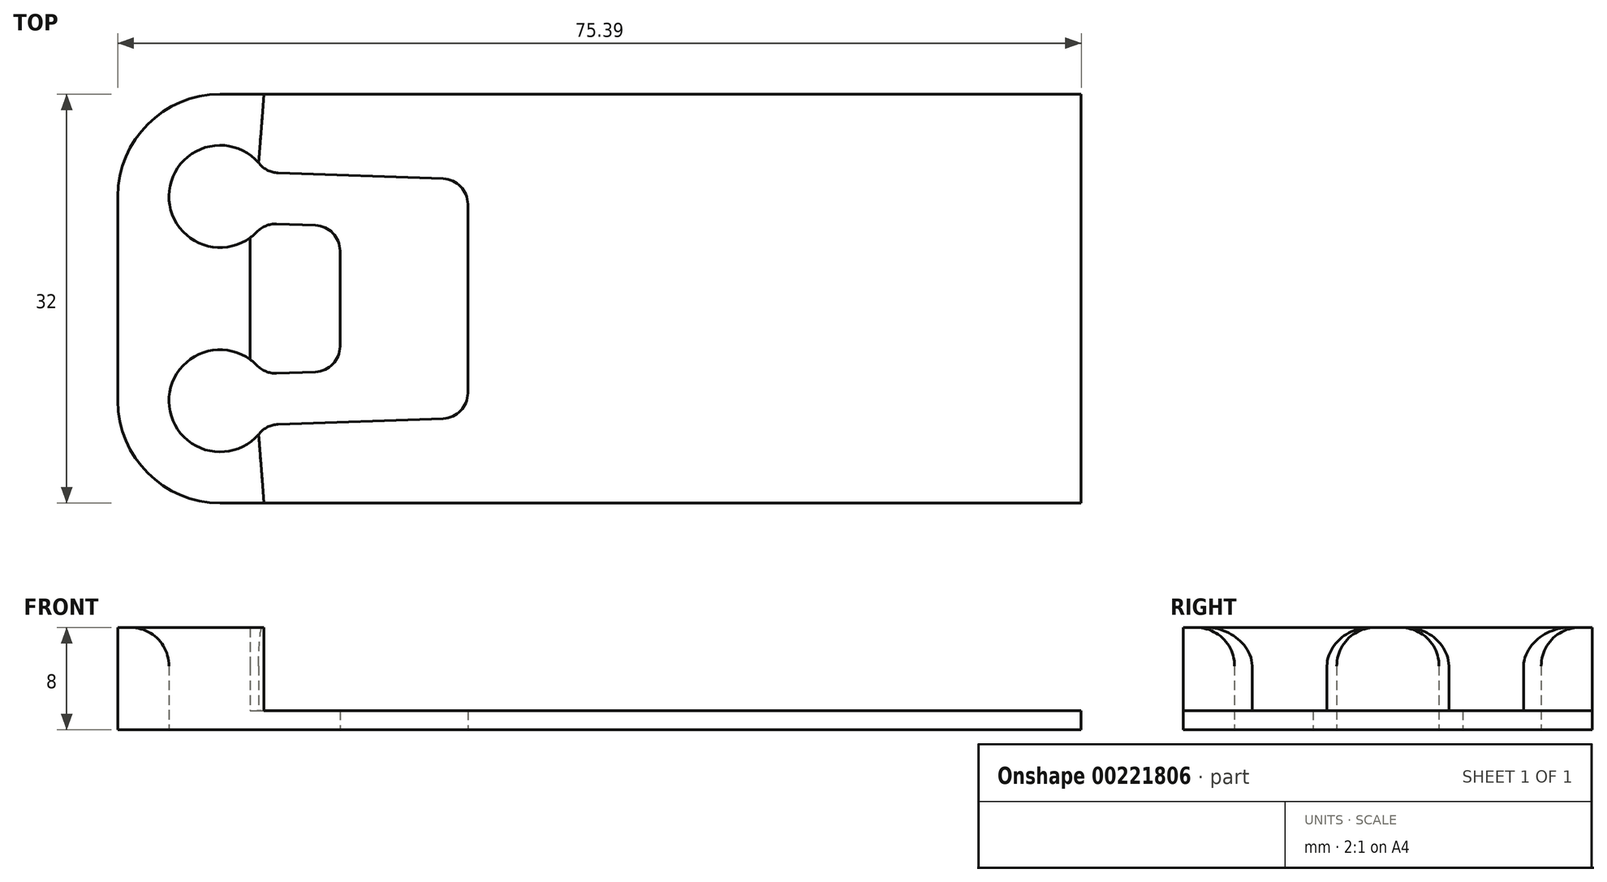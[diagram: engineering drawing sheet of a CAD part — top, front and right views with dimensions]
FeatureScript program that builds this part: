
annotation { "Feature Type Name" : "Feature", "Feature Type Description" : "" }
export const myFeature = defineFeature(function(context is Context, id is Id, definition is map)
    precondition{}
    {
        {
            var Q0;
            Q0=qCreatedBy(makeId("Top.planeOp"),FACE);
            var sketch = newSketch(context, id + "F0", { "sketchPlane" : qUnion([Q0])});
            skEllipse(sketch, "E0", {"center": v(381, 0) * mm, "majorRadius": 381 * mm, "minorRadius": 292.1 * mm, "majorAxis": v(1, 0), "construction": true});
            skSolve(sketch);
        }
        {
            var Q0;
            Q0=qCreatedBy(makeId("Top.planeOp"),FACE);
            var sketch = newSketch(context, id + "F1", { "sketchPlane" : qUnion([Q0])});
            skLineSegment(sketch, "E1", {"start": v(-10.86, 0) * mm, "end": v(-10.86, 16) * mm});
            skLineSegment(sketch, "E2", {"start": v(-10.86, 16) * mm, "end": v(64.53, 16) * mm});
            skLineSegment(sketch, "E3", {"start": v(64.53, 16) * mm, "end": v(64.53, 0) * mm});
            skCircle(sketch, "E4", {"center": v(-2.86, 8) * mm, "radius": 4 * mm});
            skLineSegment(sketch, "E5", {"start": v(-2.86, 8) * mm, "end": v(6.81, 7.66) * mm, "construction": true});
            skLineSegment(sketch, "E6", {"start": v(0.67, 9.88) * mm, "end": v(16.53, 9.32) * mm});
            skLineSegment(sketch, "E7", {"start": v(0.53, 5.88) * mm, "end": v(6.53, 5.67) * mm});
            skEllipse(sketch, "E8.0", {"center": v(381, 0) * mm, "majorRadius": 381 * mm, "minorRadius": 292.1 * mm, "majorAxis": v(1, 0), "construction": true});
            skPoint(sketch, "E9", {"position": v(0.14, 7.9) * mm});
            skLineSegment(sketch, "E10", {"start": v(6.53, 5.67) * mm, "end": v(6.53, 0) * mm});
            skLineSegment(sketch, "E11", {"start": v(16.53, 9.32) * mm, "end": v(16.53, 0) * mm});
            skLineSegment(sketch, "E12", {"start": v(20.53, 0) * mm, "end": v(20.53, 13.5) * mm, "construction": true});
            skLineSegment(sketch, "E13", {"start": v(20.53, 13.5) * mm, "end": v(60.53, 13.5) * mm, "construction": true});
            skLineSegment(sketch, "E14", {"start": v(60.53, 13.5) * mm, "end": v(60.53, 0) * mm, "construction": true});
            skLineSegment(sketch, "E15.MirrorCS", {"start": v(-10.86, 0) * mm, "end": v(-10.86, -16) * mm});
            skLineSegment(sketch, "E16.MirrorCS", {"start": v(-10.86, -16) * mm, "end": v(64.53, -16) * mm});
            skLineSegment(sketch, "E17.MirrorCS", {"start": v(64.53, -16) * mm, "end": v(64.53, 0) * mm});
            skLineSegment(sketch, "E18.MirrorCS", {"start": v(60.53, -13.5) * mm, "end": v(60.53, 0) * mm, "construction": true});
            skLineSegment(sketch, "E19.MirrorCS", {"start": v(20.53, -13.5) * mm, "end": v(60.53, -13.5) * mm, "construction": true});
            skLineSegment(sketch, "E20.MirrorCS", {"start": v(20.53, 0) * mm, "end": v(20.53, -13.5) * mm, "construction": true});
            skCircle(sketch, "E21.MirrorC", {"center": v(-2.86, -8) * mm, "radius": 4 * mm});
            skLineSegment(sketch, "E22.MirrorCS", {"start": v(0.67, -9.88) * mm, "end": v(16.53, -9.32) * mm});
            skLineSegment(sketch, "E23.MirrorCS", {"start": v(0.53, -5.88) * mm, "end": v(6.53, -5.67) * mm});
            skLineSegment(sketch, "E24.MirrorCS", {"start": v(6.53, -5.67) * mm, "end": v(6.53, 0) * mm});
            skLineSegment(sketch, "E25.MirrorCS", {"start": v(16.53, -9.32) * mm, "end": v(16.53, 0) * mm});
            skSolve(sketch);
        }
        {
            var Q0;
            Q0=makeQuery(id+"F1.imprint","IMPRINT",FACE,{"disambiguationData":[TD([[makeQuery(id+"F1.imprint","IMPRINT",EDGE,{"derivedFrom":sQuery(id+"F1.wireOp",EDGE,"E1")}),-1.0]])]});
            extrude(context, id + "F2", {"entities" : qUnion([Q0]), "depth" : 1.5 * mm});
        }
        {
            var Q0;
            Q0=qCreatedBy(makeId("Top.planeOp"),FACE);
            var sketch = newSketch(context, id + "F3", { "sketchPlane" : qUnion([Q0])});
            skEllipse(sketch, "E26.0", {"center": v(381, 0) * mm, "majorRadius": 381 * mm, "minorRadius": 292.1 * mm, "majorAxis": v(1, 0), "construction": true});
            skLineSegment(sketch, "E27.0", {"start": v(-10.86, 16) * mm, "end": v(64.53, 16) * mm});
            skLineSegment(sketch, "E28.0", {"start": v(-10.86, -16) * mm, "end": v(-10.86, 16) * mm});
            skArc(sketch, "E29.0", {"start": v(0.67, 9.88) * mm, "mid": v(-6.86, 8.14) * mm, "end": v(0.53, 5.88) * mm});
            skLineSegment(sketch, "E30", {"start": v(0.57, 16) * mm, "end": v(0.16, 10.62) * mm});
            skLineSegment(sketch, "E31.MirrorCS", {"start": v(0.57, -16) * mm, "end": v(0.16, -10.62) * mm});
            skArc(sketch, "E32.0", {"start": v(0.67, -9.88) * mm, "mid": v(-6.86, -8.14) * mm, "end": v(0.53, -5.88) * mm});
            skLineSegment(sketch, "E33.0", {"start": v(-10.86, -16) * mm, "end": v(64.53, -16) * mm});
            skLineSegment(sketch, "E34", {"start": v(-0.5, 4.77) * mm, "end": v(-0.5, -4.77) * mm});
            skSolve(sketch);
        }
        {
            var Q0;
            {var subQ3=sQuery(id+"F3.wireOp",EDGE,"E28.0");Q0=makeQuery(id+"F3.imprint","IMPRINT",FACE,{"disambiguationData":[TD([[makeQuery(id+"F3.imprint","IMPRINT",EDGE,{"derivedFrom":subQ3}),-1.0]])]});}
            extrude(context, id + "F4", {"entities" : qUnion([Q0]), "operationType" : NewBodyOperationType.ADD, "depth" : 8 * mm});
        }
        {
            var Q0;
            Q0=makeQuery(id+"F4.opExtrude","CAP_EDGE",EDGE,{"disambiguationData":[OSD([sQuery(id+"F3.wireOp",EDGE,"E29.0")])],"isStart":false});
            var Q1;
            Q1=makeQuery(id+"F4.opExtrude","CAP_EDGE",EDGE,{"disambiguationData":[OSD([sQuery(id+"F3.wireOp",EDGE,"E32.0")])],"isStart":false});
            fillet(context, id + "F5", {"entities" : qUnion([Q0, Q1]), "radius" : 3 * mm, "tangentPropagation" : true, "allowEdgeOverflow" : false});
        }
        {
            var Q0;
            Q0=makeQuery(id+"F2.opExtrude","SWEPT_EDGE",EDGE,{"disambiguationData":[OSD([sQuery(id+"F1.wireOp",EDGE,"E4"),sQuery(id+"F1.wireOp",EDGE,"E7")])]});
            var Q1;
            Q1=makeQuery(id+"F2.opExtrude","SWEPT_EDGE",EDGE,{"disambiguationData":[OSD([sQuery(id+"F1.wireOp",EDGE,"E21.MirrorC"),sQuery(id+"F1.wireOp",EDGE,"E23.MirrorCS")])]});
            var Q2;
            Q2=makeQuery(id+"F2.opExtrude","SWEPT_EDGE",EDGE,{"disambiguationData":[OSD([sQuery(id+"F1.wireOp",EDGE,"E6"),sQuery(id+"F1.wireOp",EDGE,"E11")])]});
            var Q3;
            Q3=makeQuery(id+"F2.opExtrude","SWEPT_EDGE",EDGE,{"disambiguationData":[OSD([sQuery(id+"F1.wireOp",EDGE,"E22.MirrorCS"),sQuery(id+"F1.wireOp",EDGE,"E25.MirrorCS")])]});
            var Q4;
            Q4=makeQuery(id+"F2.opExtrude","SWEPT_EDGE",EDGE,{"disambiguationData":[OSD([sQuery(id+"F1.wireOp",EDGE,"E21.MirrorC"),sQuery(id+"F1.wireOp",EDGE,"E22.MirrorCS")])]});
            var Q5;
            Q5=makeQuery(id+"F2.opExtrude","SWEPT_EDGE",EDGE,{"disambiguationData":[OSD([sQuery(id+"F1.wireOp",EDGE,"E4"),sQuery(id+"F1.wireOp",EDGE,"E6")])]});
            var Q6;
            Q6=makeQuery(id+"F2.opExtrude","SWEPT_EDGE",EDGE,{"disambiguationData":[OSD([sQuery(id+"F1.wireOp",EDGE,"E7"),sQuery(id+"F1.wireOp",EDGE,"E10")])]});
            var Q7;
            Q7=makeQuery(id+"F2.opExtrude","SWEPT_EDGE",EDGE,{"disambiguationData":[OSD([sQuery(id+"F1.wireOp",EDGE,"E23.MirrorCS"),sQuery(id+"F1.wireOp",EDGE,"E24.MirrorCS")])]});
            fillet(context, id + "F6", {"entities" : qUnion([Q0, Q1, Q2, Q3, Q4, Q5, Q6, Q7]), "radius" : 2 * mm, "tangentPropagation" : true, "allowEdgeOverflow" : false});
        }
        {
            var Q0;
            Q0=makeQuery(id+"F4.boolean.opBoolean","MERGE",EDGE,{"derivedFrom":[makeQuery(id+"F2.opExtrude","SWEPT_EDGE",EDGE,{"disambiguationData":[OSD([sQuery(id+"F1.wireOp",EDGE,"E1"),sQuery(id+"F1.wireOp",EDGE,"E2")])]}),makeQuery(id+"F4.opExtrude","SWEPT_EDGE",EDGE,{"disambiguationData":[OSD([sQuery(id+"F3.wireOp",EDGE,"E27.0"),sQuery(id+"F3.wireOp",EDGE,"E28.0")])]})]});
            var Q1;
            Q1=makeQuery(id+"F4.boolean.opBoolean","MERGE",EDGE,{"derivedFrom":[makeQuery(id+"F2.opExtrude","SWEPT_EDGE",EDGE,{"disambiguationData":[OSD([sQuery(id+"F1.wireOp",EDGE,"E15.MirrorCS"),sQuery(id+"F1.wireOp",EDGE,"E16.MirrorCS")])]}),makeQuery(id+"F4.opExtrude","SWEPT_EDGE",EDGE,{"disambiguationData":[OSD([sQuery(id+"F3.wireOp",EDGE,"E28.0"),sQuery(id+"F3.wireOp",EDGE,"E33.0")])]})]});
            fillet(context, id + "F7", {"entities" : qUnion([Q0, Q1]), "radius" : 8 * mm, "tangentPropagation" : true, "allowEdgeOverflow" : false});
        }
    });
